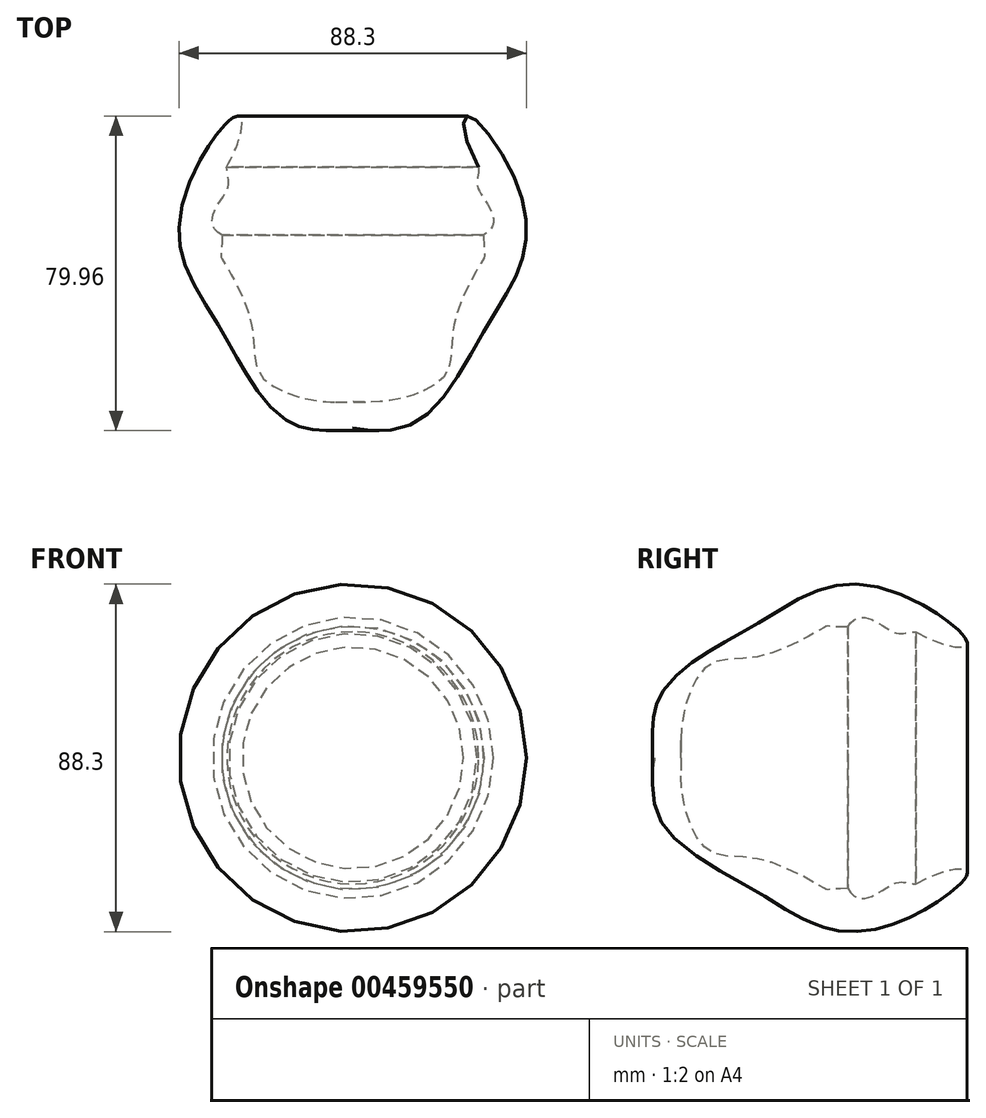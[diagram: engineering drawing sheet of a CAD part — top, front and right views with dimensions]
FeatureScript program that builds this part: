
annotation { "Feature Type Name" : "Feature", "Feature Type Description" : "" }
export const myFeature = defineFeature(function(context is Context, id is Id, definition is map)
    precondition{}
    {
        {
            var Q0;
            Q0=qCreatedBy(makeId("Top.planeOp"),FACE);
            var sketch = newSketch(context, id + "F0", { "sketchPlane" : qUnion([Q0])});
            skLineSegment(sketch, "E0", {"start": v(0, 55.63) * mm, "end": v(0, -56.24) * mm});
            skFitSpline(sketch, "E1", {"points": [v(-0.75, -48.82) * mm, v(16.76, -47.1) * mm, v(33.53, -23.93) * mm, v(43.28, -5.39) * mm, v(40.84, 15.09) * mm, v(29.26, 30.33) * mm, v(32, 17.35) * mm], "startDerivative": vector(103.2, -19.83) * mm, "endDerivative": vector(92.57, -167.25) * mm});
            skFitSpline(sketch, "E2", {"points": [v(32, 17.35) * mm, v(32, 11.48) * mm, v(33.22, 0) * mm], "startDerivative": vector(0, -19.34) * mm, "endDerivative": vector(-28.97, -16.33) * mm});
            skFitSpline(sketch, "E3", {"points": [v(33.22, 0) * mm, v(33.22, -5.94) * mm, v(25.9, -21.8) * mm, v(23.47, -35.5) * mm, v(10.06, -41.91) * mm, v(0, -42.21) * mm], "startDerivative": vector(0, -126.57) * mm, "endDerivative": vector(-51.07, 2.82) * mm});
            skPoint(sketch, "E4.1.internal.orphan", {"position": v(-11.86, -48.82) * mm});
            skSolve(sketch);
        }
        {
            var Q0;
            {var subQ0=sQuery(id+"F0.wireOp",EDGE,"E1");Q0=makeQuery(id+"F0.imprint","IMPRINT",FACE,{"disambiguationData":[TD([[makeQuery(id+"F0.imprint","IMPRINT",EDGE,{"derivedFrom":subQ0}),1.0]])]});}
            var Q1;
            Q1=sQuery(id+"F0.wireOp",EDGE,"E0");
            revolve(context, id + "F1", {"entities" : qUnion([Q0]), "axis" : qUnion([Q1]), "revolveType" : RevolveType.FULL});
        }
    });
